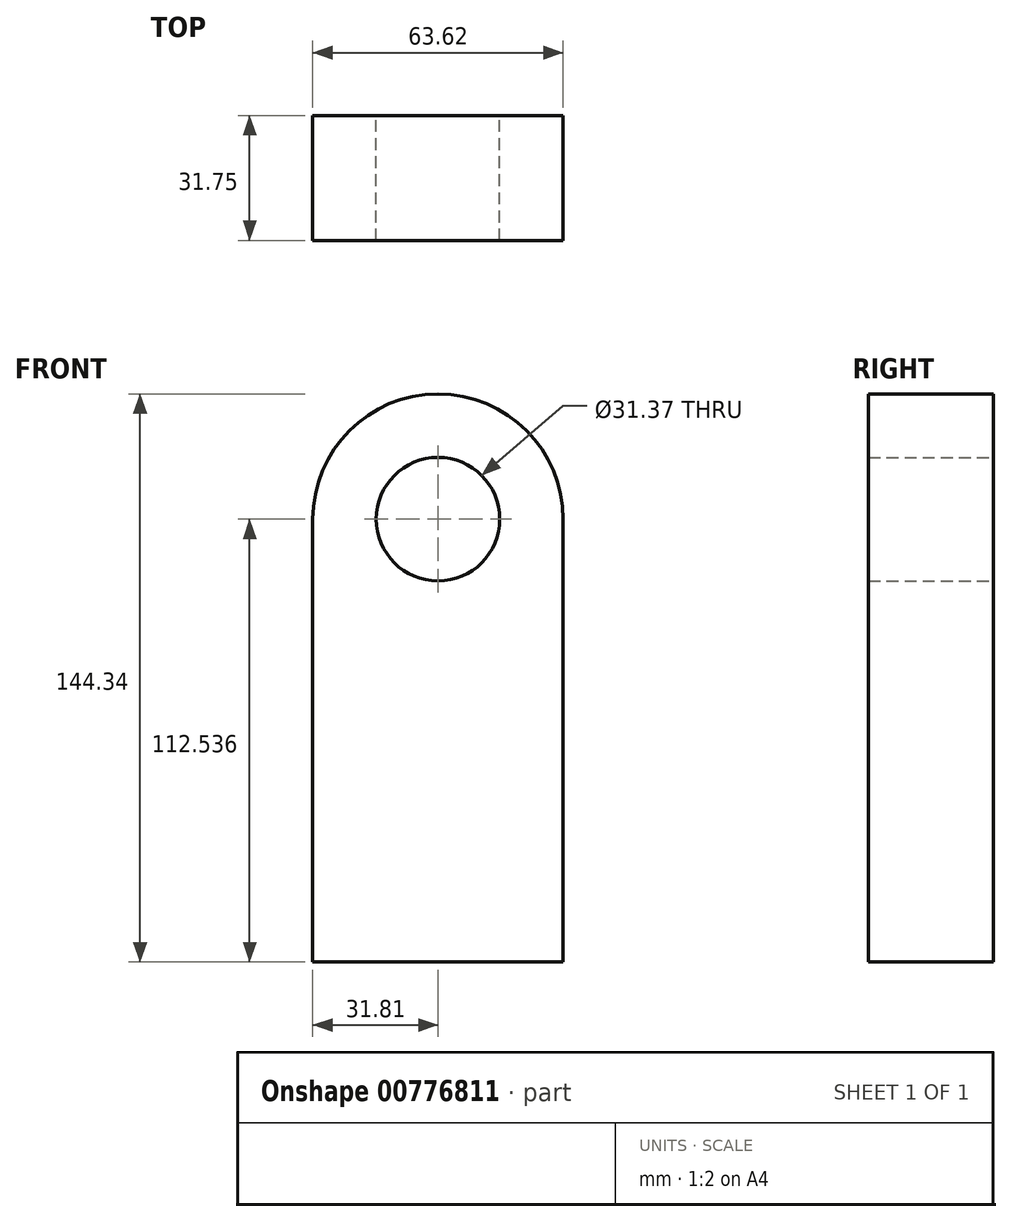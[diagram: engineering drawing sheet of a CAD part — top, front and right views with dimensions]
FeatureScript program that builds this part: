
annotation { "Feature Type Name" : "Feature", "Feature Type Description" : "" }
export const myFeature = defineFeature(function(context is Context, id is Id, definition is map)
    precondition{}
    {
        {
            var Q0;
            Q0=qCreatedBy(makeId("Front.planeOp"),FACE);
            var sketch = newSketch(context, id + "F0", { "sketchPlane" : qUnion([Q0])});
            skLineSegment(sketch, "E0.top", {"start": v(31.8, -56.27) * mm, "end": v(-31.8, -56.27) * mm});
            skLineSegment(sketch, "E0.left", {"start": v(31.8, 56.27) * mm, "end": v(31.8, -56.27) * mm});
            skLineSegment(sketch, "E0.right", {"start": v(-31.8, 56.27) * mm, "end": v(-31.8, -56.27) * mm});
            skPoint(sketch, "E0.middle", {"position": v(0, 0) * mm});
            skArc(sketch, "E1", {"start": v(31.8, 56.27) * mm, "mid": v(0, 88.07) * mm, "end": v(-31.8, 56.27) * mm});
            skCircle(sketch, "E2", {"center": v(0, 56.27) * mm, "radius": 15.69 * mm});
            skSolve(sketch);
        }
        {
            var Q0;
            Q0 = qSketchRegion(id + "F0", true);
            extrude(context, id + "F1", {"entities" : qUnion([Q0]), "depth" : 31.75 * mm, "offsetDistance" : 25.4 * mm});
        }
    });
